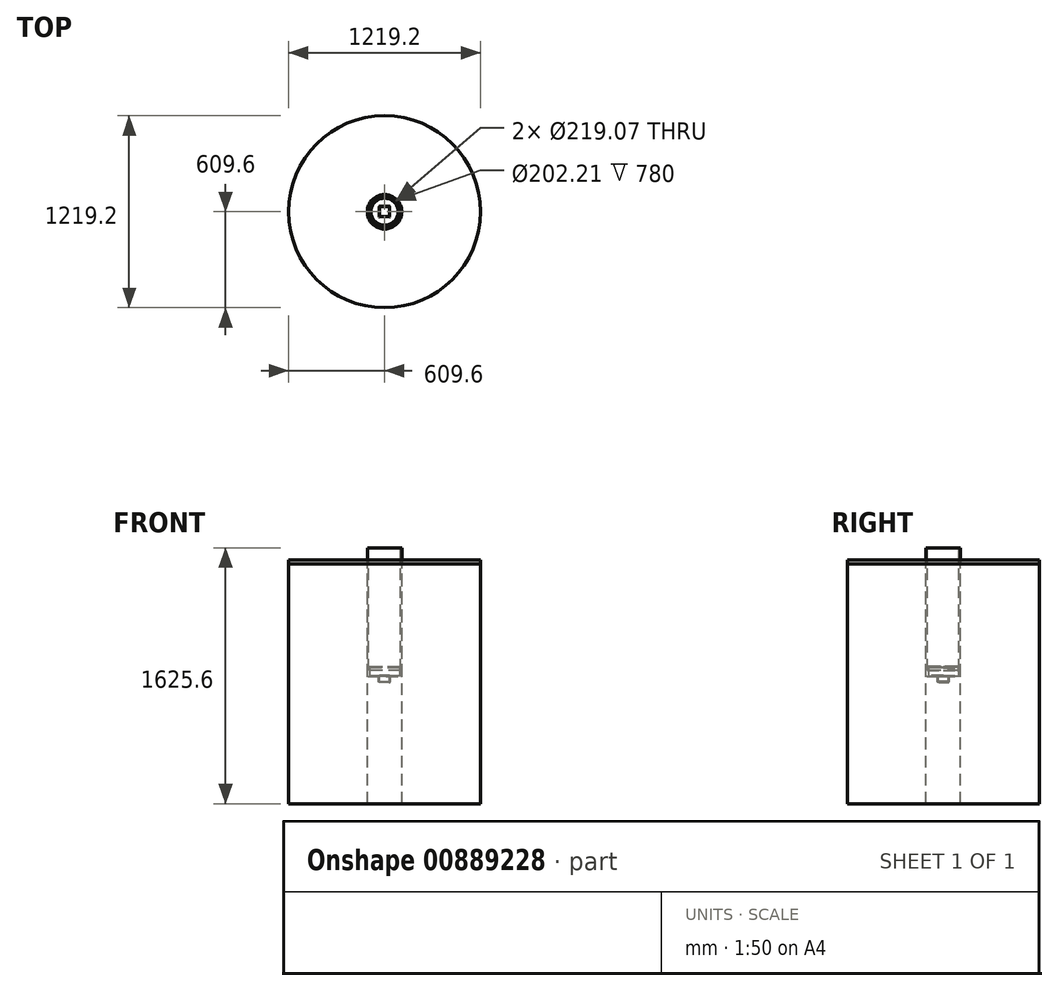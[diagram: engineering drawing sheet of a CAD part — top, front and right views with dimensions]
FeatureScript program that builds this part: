
annotation { "Feature Type Name" : "Feature", "Feature Type Description" : "" }
export const myFeature = defineFeature(function(context is Context, id is Id, definition is map)
    precondition{}
    {
        {
            var Q0;
            Q0=qCreatedBy(makeId("Top.planeOp"),FACE);
            var sketch = newSketch(context, id + "F0", { "sketchPlane" : qUnion([Q0])});
            skCircle(sketch, "E0", {"center": v(0, 0) * mm, "radius": 609.6 * mm});
            skCircle(sketch, "E1", {"center": v(0, 0) * mm, "radius": 109.54 * mm});
            skSolve(sketch);
        }
        {
            var Q0;
            Q0=makeQuery(id+"F0.imprint","IMPRINT",FACE,{"disambiguationData":[TD([[makeQuery(id+"F0.imprint","IMPRINT",EDGE,{"derivedFrom":sQuery(id+"F0.wireOp",EDGE,"E0")}),1.0]])]});
            extrude(context, id + "F1", {"entities" : qUnion([Q0]), "depth" : 25.4 * mm, "offsetDistance" : 25.4 * mm});
        }
        {
            var Q0;
            Q0=makeQuery(id+"F1.opExtrude","CAP_FACE",FACE,{"disambiguationData":[OSD([sQuery(id+"F0.wireOp",EDGE,"E0"),sQuery(id+"F0.wireOp",EDGE,"E1")])],"isStart":true});
            extrude(context, id + "F2", {"entities" : qUnion([Q0]), "depth" : 1524 * mm, "offsetDistance" : 25.4 * mm});
        }
        {
            var Q0;
            Q0=makeQuery(id+"F1.opExtrude","CAP_FACE",FACE,{"disambiguationData":[OSD([sQuery(id+"F0.wireOp",EDGE,"E0"),sQuery(id+"F0.wireOp",EDGE,"E1")])],"isStart":false});
            cPlane(context, id + "F3", {"entities" : qUnion([Q0]), "cplaneType" : CPlaneType.OFFSET, "offset" : 76.2 * mm, "width" : 152.4 * mm, "height" : 152.4 * mm});
        }
        {
            var Q0;
            Q0=qCreatedBy(id+"F3.planeOp",FACE);
            var sketch = newSketch(context, id + "F4", { "sketchPlane" : qUnion([Q0])});
            skCircle(sketch, "E2", {"center": v(0, 0) * mm, "radius": 109.54 * mm});
            skCircle(sketch, "E3", {"center": v(0, 0) * mm, "radius": 101.1 * mm});
            skSolve(sketch);
        }
        {
            var Q0;
            Q0=makeQuery(id+"F4.imprint","IMPRINT",FACE,{"disambiguationData":[TD([[makeQuery(id+"F4.imprint","IMPRINT",EDGE,{"derivedFrom":sQuery(id+"F4.wireOp",EDGE,"E2")}),1.0]])]});
            extrude(context, id + "F5", {"entities" : qUnion([Q0]), "oppositeDirection" : true, "depth" : (250 * mm * 3) + 30 * mm, "offsetDistance" : 25.4 * mm});
        }
        {
            var Q0;
            Q0=makeQuery(id+"F5.opExtrude","CAP_FACE",FACE,{"disambiguationData":[OSD([sQuery(id+"F4.wireOp",EDGE,"E2"),sQuery(id+"F4.wireOp",EDGE,"E3")])],"isStart":false});
            var sketch = newSketch(context, id + "F6", { "sketchPlane" : qUnion([Q0])});
            skCircle(sketch, "E4", {"center": v(0, 0) * mm, "radius": 101.1 * mm});
            skCircle(sketch, "E5", {"center": v(0, 0) * mm, "radius": 109.54 * mm});
            skSolve(sketch);
        }
        {
            var Q0;
            Q0=makeQuery(id+"F6.imprint","IMPRINT",FACE,{"disambiguationData":[TD([[makeQuery(id+"F6.imprint","IMPRINT",EDGE,{"derivedFrom":sQuery(id+"F6.wireOp",EDGE,"E4")}),1.0]])]});
            var Q1;
            Q1=makeQuery(id+"F6.imprint","IMPRINT",FACE,{"disambiguationData":[TD([[makeQuery(id+"F6.imprint","IMPRINT",EDGE,{"derivedFrom":sQuery(id+"F6.wireOp",EDGE,"E4")}),-1.0]])]});
            extrude(context, id + "F7", {"entities" : qUnion([Q0, Q1]), "depth" : 38.1 * mm, "offsetDistance" : 25.4 * mm});
        }
        {
            var Q0;
            Q0=makeQuery(id+"F6.imprint","IMPRINT",FACE,{"disambiguationData":[TD([[makeQuery(id+"F6.imprint","IMPRINT",EDGE,{"derivedFrom":sQuery(id+"F6.wireOp",EDGE,"E4")}),-1.0]])]});
            extrude(context, id + "F8", {"entities" : qUnion([Q0]), "operationType" : NewBodyOperationType.ADD, "oppositeDirection" : true, "depth" : 25.4 * mm, "offsetDistance" : 25.4 * mm, "hasDraft" : true, "draftAngle" : 1 * degree, "draftPullDirection" : true});
        }
        {
            var Q0;
            Q0=makeQuery(id+"F7.opExtrude","CAP_FACE",FACE,{"disambiguationData":[OSD([sQuery(id+"F6.wireOp",EDGE,"E5")])],"isStart":false});
            var sketch = newSketch(context, id + "F9", { "sketchPlane" : qUnion([Q0])});
            skLineSegment(sketch, "E6.bottom", {"start": v(38.1, 38.1) * mm, "end": v(-38.1, 38.1) * mm});
            skLineSegment(sketch, "E6.top", {"start": v(38.1, -38.1) * mm, "end": v(-38.1, -38.1) * mm});
            skLineSegment(sketch, "E6.left", {"start": v(38.1, 38.1) * mm, "end": v(38.1, -38.1) * mm});
            skLineSegment(sketch, "E6.right", {"start": v(-38.1, 38.1) * mm, "end": v(-38.1, -38.1) * mm});
            skPoint(sketch, "E6.middle", {"position": v(0, 0) * mm});
            skSolve(sketch);
        }
        {
            var Q0;
            Q0=makeQuery(id+"F9.imprint","IMPRINT",FACE,{"disambiguationData":[TD([[makeQuery(id+"F9.imprint","IMPRINT",EDGE,{"derivedFrom":sQuery(id+"F9.wireOp",EDGE,"E6.bottom")}),1.0]])]});
            extrude(context, id + "F10", {"entities" : qUnion([Q0]), "operationType" : NewBodyOperationType.ADD, "depth" : 38.1 * mm, "offsetDistance" : 25.4 * mm});
        }
        {
            var Q0;
            Q0=makeQuery(id+"F10.opExtrude","CAP_EDGE",EDGE,{"disambiguationData":[OSD([sQuery(id+"F9.wireOp",EDGE,"E6.top")])],"isStart":true});
            var Q1;
            Q1=makeQuery(id+"F10.opExtrude","CAP_EDGE",EDGE,{"disambiguationData":[OSD([sQuery(id+"F9.wireOp",EDGE,"E6.left")])],"isStart":true});
            var Q2;
            Q2=makeQuery(id+"F10.opExtrude","CAP_EDGE",EDGE,{"disambiguationData":[OSD([sQuery(id+"F9.wireOp",EDGE,"E6.right")])],"isStart":true});
            var Q3;
            Q3=makeQuery(id+"F10.opExtrude","CAP_EDGE",EDGE,{"disambiguationData":[OSD([sQuery(id+"F9.wireOp",EDGE,"E6.bottom")])],"isStart":true});
            var Q4;
            Q4=makeQuery(id+"F10.opExtrude","CAP_EDGE",EDGE,{"disambiguationData":[OSD([sQuery(id+"F9.wireOp",EDGE,"E6.bottom")])],"isStart":false});
            var Q5;
            Q5=makeQuery(id+"F10.opExtrude","CAP_EDGE",EDGE,{"disambiguationData":[OSD([sQuery(id+"F9.wireOp",EDGE,"E6.left")])],"isStart":false});
            var Q6;
            Q6=makeQuery(id+"F10.opExtrude","CAP_EDGE",EDGE,{"disambiguationData":[OSD([sQuery(id+"F9.wireOp",EDGE,"E6.top")])],"isStart":false});
            var Q7;
            Q7=makeQuery(id+"F10.opExtrude","CAP_EDGE",EDGE,{"disambiguationData":[OSD([sQuery(id+"F9.wireOp",EDGE,"E6.right")])],"isStart":false});
            fillet(context, id + "F11", {"entities" : qUnion([Q0, Q1, Q2, Q3, Q4, Q5, Q6, Q7]), "radius" : 9.52 * mm, "tangentPropagation" : true, "allowEdgeOverflow" : false});
        }
        {
            var Q0;
            Q0=makeQuery(id+"F10.opExtrude","SWEPT_EDGE",EDGE,{"disambiguationData":[OSD([sQuery(id+"F9.wireOp",EDGE,"E6.top"),sQuery(id+"F9.wireOp",EDGE,"E6.right")])]});
            var Q1;
            Q1=makeQuery(id+"F10.opExtrude","SWEPT_EDGE",EDGE,{"disambiguationData":[OSD([sQuery(id+"F9.wireOp",EDGE,"E6.top"),sQuery(id+"F9.wireOp",EDGE,"E6.left")])]});
            var Q2;
            Q2=makeQuery(id+"F10.opExtrude","SWEPT_EDGE",EDGE,{"disambiguationData":[OSD([sQuery(id+"F9.wireOp",EDGE,"E6.bottom"),sQuery(id+"F9.wireOp",EDGE,"E6.left")])]});
            var Q3;
            Q3=makeQuery(id+"F10.opExtrude","SWEPT_EDGE",EDGE,{"disambiguationData":[OSD([sQuery(id+"F9.wireOp",EDGE,"E6.bottom"),sQuery(id+"F9.wireOp",EDGE,"E6.right")])]});
            fillet(context, id + "F12", {"entities" : qUnion([Q0, Q1, Q2, Q3]), "radius" : 5.08 * mm, "tangentPropagation" : true, "allowEdgeOverflow" : false});
        }
        {
            var Q0;
            Q0=makeQuery(id+"F7.opExtrude","CAP_EDGE",EDGE,{"disambiguationData":[OSD([sQuery(id+"F6.wireOp",EDGE,"E5")])],"isStart":false});
            var Q1;
            Q1=makeQuery(id+"F8.opExtrude","CAP_EDGE",EDGE,{"disambiguationData":[OSD([sQuery(id+"F6.wireOp",EDGE,"E4")])],"isStart":false});
            chamfer(context, id + "F13", {"entities" : qUnion([Q0, Q1]), "width" : 5.08 * mm, "tangentPropagation" : true});
        }
        {
            var Q0;
            Q0=makeQuery(id+"F8.opExtrude","CAP_FACE",FACE,{"disambiguationData":[OSD([sQuery(id+"F6.wireOp",EDGE,"E4")])],"isStart":false});
            shell(context, id + "F14", {"entities" : qUnion([Q0]), "thickness" : 6.35 * mm});
        }
    });
